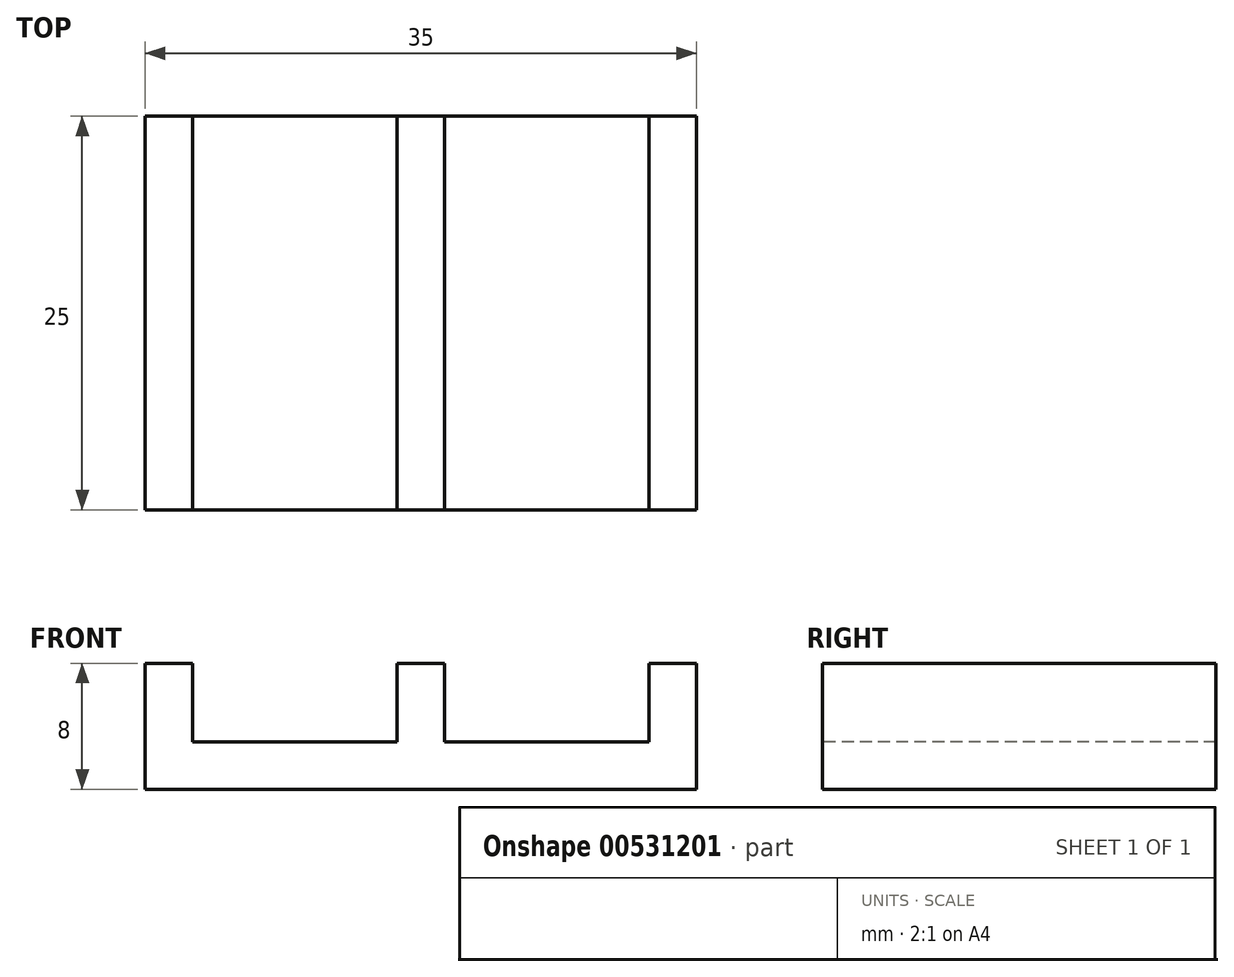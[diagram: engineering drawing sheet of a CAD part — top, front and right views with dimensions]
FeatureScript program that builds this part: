
annotation { "Feature Type Name" : "Feature", "Feature Type Description" : "" }
export const myFeature = defineFeature(function(context is Context, id is Id, definition is map)
    precondition{}
    {
        {
            var Q0;
            Q0=qCreatedBy(makeId("Top.planeOp"),FACE);
            var sketch = newSketch(context, id + "F0", { "sketchPlane" : qUnion([Q0])});
            skLineSegment(sketch, "E0.bottom", {"start": v(23.67, -41.2) * mm, "end": v(58.67, -41.2) * mm});
            skLineSegment(sketch, "E0.top", {"start": v(23.67, -66.2) * mm, "end": v(58.67, -66.2) * mm});
            skLineSegment(sketch, "E0.left", {"start": v(23.67, -41.2) * mm, "end": v(23.67, -66.2) * mm});
            skLineSegment(sketch, "E0.right", {"start": v(58.67, -41.2) * mm, "end": v(58.67, -66.2) * mm});
            skSolve(sketch);
        }
        {
            var Q0;
            Q0=makeQuery(id+"F0.imprint","IMPRINT",FACE,{"disambiguationData":[TD([[makeQuery(id+"F0.imprint","IMPRINT",EDGE,{"derivedFrom":sQuery(id+"F0.wireOp",EDGE,"E0.bottom")}),-1.0]])]});
            extrude(context, id + "F1", {"entities" : qUnion([Q0]), "depth" : 3 * mm, "offsetDistance" : 25 * mm});
        }
        {
            var Q0;
            Q0=makeQuery(id+"F1.opExtrude","CAP_FACE",FACE,{"disambiguationData":[OSD([sQuery(id+"F0.wireOp",EDGE,"E0.bottom"),sQuery(id+"F0.wireOp",EDGE,"E0.top"),sQuery(id+"F0.wireOp",EDGE,"E0.left"),sQuery(id+"F0.wireOp",EDGE,"E0.right")])],"isStart":false});
            var sketch = newSketch(context, id + "F2", { "sketchPlane" : qUnion([Q0])});
            skLineSegment(sketch, "E1", {"start": v(23.67, -53.7) * mm, "end": v(58.67, -53.7) * mm});
            skLineSegment(sketch, "E2", {"start": v(41.17, -41.2) * mm, "end": v(41.17, -66.2) * mm});
            skLineSegment(sketch, "E3.bottom", {"start": v(42.67, -66.2) * mm, "end": v(39.67, -66.2) * mm});
            skLineSegment(sketch, "E3.top", {"start": v(42.67, -41.2) * mm, "end": v(39.67, -41.2) * mm});
            skLineSegment(sketch, "E3.left", {"start": v(42.67, -66.2) * mm, "end": v(42.67, -41.2) * mm});
            skLineSegment(sketch, "E3.right", {"start": v(39.67, -66.2) * mm, "end": v(39.67, -41.2) * mm});
            skPoint(sketch, "E3.middle", {"position": v(41.17, -53.7) * mm});
            skSolve(sketch);
        }
        {
            var Q0;
            Q0 = qSketchRegion(id + "F2", true);
            extrude(context, id + "F3", {"entities" : qUnion([Q0]), "operationType" : NewBodyOperationType.ADD, "depth" : 5 * mm, "offsetDistance" : 25 * mm});
        }
        {
            var Q0;
            {var subQ0=sQuery(id+"F0.wireOp",EDGE,"E0.left");var subQ1=sQuery(id+"F0.wireOp",EDGE,"E0.top");var subQ2=sQuery(id+"F0.wireOp",EDGE,"E0.bottom");Q0=makeQuery(id+"F3.boolean.opBoolean","SPLIT",FACE,{"disambiguationData":[TD([makeQuery(id+"F1.opExtrude","SWEPT_FACE",FACE,{"disambiguationData":[OSD([subQ0])]})])],"derivedFrom":makeQuery(id+"F1.opExtrude","CAP_FACE",FACE,{"disambiguationData":[OSD([subQ2,subQ1,subQ0,sQuery(id+"F0.wireOp",EDGE,"E0.right")])],"isStart":false})});}
            var sketch = newSketch(context, id + "F4", { "sketchPlane" : qUnion([Q0])});
            skLineSegment(sketch, "E4.bottom", {"start": v(23.67, -41.2) * mm, "end": v(26.67, -41.2) * mm});
            skLineSegment(sketch, "E4.top", {"start": v(23.67, -66.2) * mm, "end": v(26.67, -66.2) * mm});
            skLineSegment(sketch, "E4.left", {"start": v(23.67, -41.2) * mm, "end": v(23.67, -66.2) * mm});
            skLineSegment(sketch, "E4.right", {"start": v(26.67, -41.2) * mm, "end": v(26.67, -66.2) * mm});
            skSolve(sketch);
        }
        {
            var Q0;
            Q0 = qSketchRegion(id + "F4", true);
            extrude(context, id + "F5", {"entities" : qUnion([Q0]), "operationType" : NewBodyOperationType.ADD, "depth" : 5 * mm, "offsetDistance" : 25 * mm});
        }
        {
            var Q0;
            {var subQ0=sQuery(id+"F0.wireOp",EDGE,"E0.top");var subQ1=sQuery(id+"F0.wireOp",EDGE,"E0.right");var subQ2=sQuery(id+"F0.wireOp",EDGE,"E0.bottom");Q0=makeQuery(id+"F3.boolean.opBoolean","SPLIT",FACE,{"disambiguationData":[TD([makeQuery(id+"F1.opExtrude","SWEPT_FACE",FACE,{"disambiguationData":[OSD([subQ1])]})])],"derivedFrom":makeQuery(id+"F1.opExtrude","CAP_FACE",FACE,{"disambiguationData":[OSD([subQ2,subQ0,sQuery(id+"F0.wireOp",EDGE,"E0.left"),subQ1])],"isStart":false})});}
            var sketch = newSketch(context, id + "F6", { "sketchPlane" : qUnion([Q0])});
            skLineSegment(sketch, "E5.bottom", {"start": v(58.67, -41.2) * mm, "end": v(55.67, -41.2) * mm});
            skLineSegment(sketch, "E5.top", {"start": v(58.67, -66.2) * mm, "end": v(55.67, -66.2) * mm});
            skLineSegment(sketch, "E5.left", {"start": v(58.67, -41.2) * mm, "end": v(58.67, -66.2) * mm});
            skLineSegment(sketch, "E5.right", {"start": v(55.67, -41.2) * mm, "end": v(55.67, -66.2) * mm});
            skSolve(sketch);
        }
        {
            var Q0;
            Q0=makeQuery(id+"F6.imprint","IMPRINT",FACE,{"disambiguationData":[TD([[makeQuery(id+"F6.imprint","IMPRINT",EDGE,{"derivedFrom":sQuery(id+"F6.wireOp",EDGE,"E5.bottom")}),-1.0]])]});
            extrude(context, id + "F7", {"entities" : qUnion([Q0]), "operationType" : NewBodyOperationType.ADD, "depth" : 5 * mm, "offsetDistance" : 25 * mm});
        }
    });
